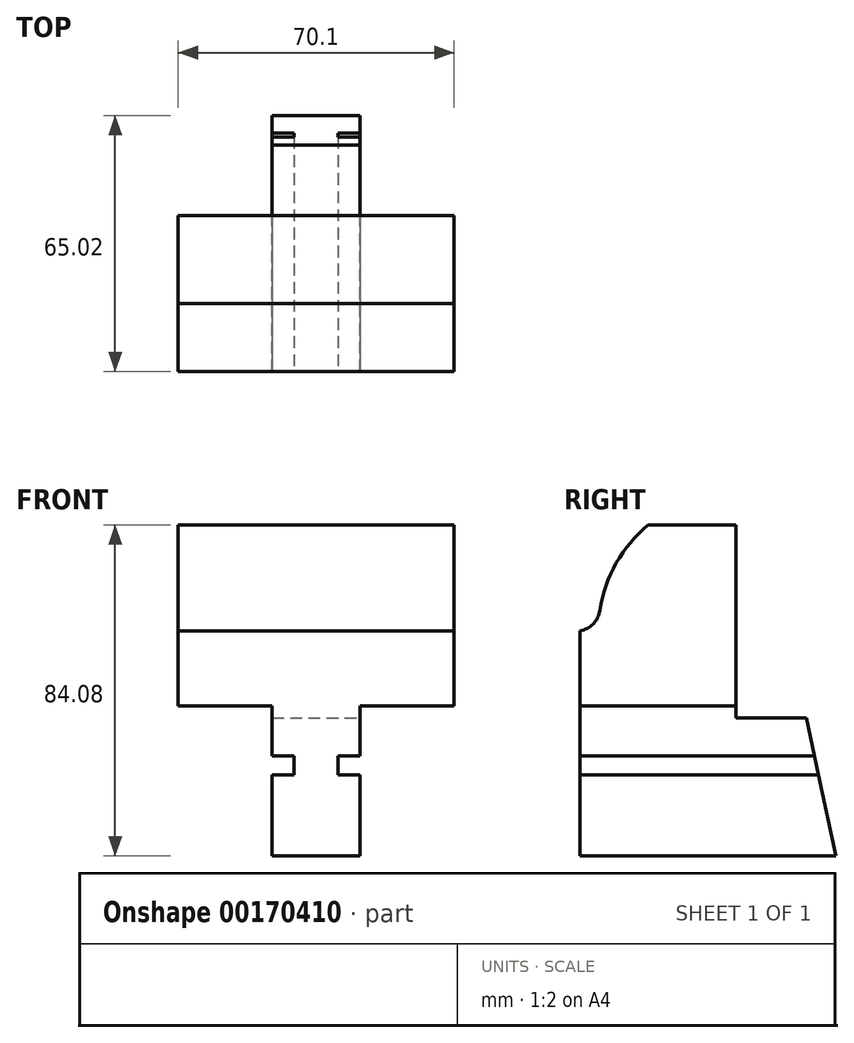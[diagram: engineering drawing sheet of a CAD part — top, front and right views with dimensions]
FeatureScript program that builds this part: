
annotation { "Feature Type Name" : "Feature", "Feature Type Description" : "" }
export const myFeature = defineFeature(function(context is Context, id is Id, definition is map)
    precondition{}
    {
        {
            var Q0;
            Q0=qCreatedBy(makeId("Right.planeOp"),FACE);
            var sketch = newSketch(context, id + "F0", { "sketchPlane" : qUnion([Q0])});
            skLineSegment(sketch, "E0.bottom", {"start": v(32.51, 42.04) * mm, "end": v(-32.51, 42.04) * mm});
            skLineSegment(sketch, "E0.top", {"start": v(32.51, -42.04) * mm, "end": v(-32.51, -42.04) * mm});
            skLineSegment(sketch, "E0.left", {"start": v(32.51, 42.04) * mm, "end": v(32.51, -42.04) * mm});
            skLineSegment(sketch, "E0.right", {"start": v(-32.51, 42.04) * mm, "end": v(-32.51, -42.04) * mm});
            skPoint(sketch, "E0.middle", {"position": v(0, 0) * mm});
            skSolve(sketch);
        }
        {
            var Q0;
            Q0=makeQuery(id+"F0.imprint","IMPRINT",FACE,{"disambiguationData":[TD([[makeQuery(id+"F0.imprint","IMPRINT",EDGE,{"derivedFrom":sQuery(id+"F0.wireOp",EDGE,"E0.bottom")}),1.0]])]});
            extrude(context, id + "F1", {"entities" : qUnion([Q0]), "depth" : 35.05 * mm, "hasSecondDirection" : true, "secondDirectionOppositeDirection" : true, "secondDirectionDepth" : 35.05 * mm});
        }
        {
            var Q0;
            Q0=qCreatedBy(makeId("Front.planeOp"),FACE);
            var sketch = newSketch(context, id + "F2", { "sketchPlane" : qUnion([Q0])});
            skLineSegment(sketch, "E1.bottom", {"start": v(-11.18, -3.94) * mm, "end": v(-78.23, -3.94) * mm});
            skLineSegment(sketch, "E1.top", {"start": v(-11.18, -87.81) * mm, "end": v(-78.23, -87.81) * mm});
            skLineSegment(sketch, "E1.left", {"start": v(-11.18, -3.94) * mm, "end": v(-11.18, -16.64) * mm});
            skLineSegment(sketch, "E1.right", {"start": v(-78.23, -3.94) * mm, "end": v(-78.23, -87.81) * mm});
            skLineSegment(sketch, "E2.bottom", {"start": v(11.18, -3.94) * mm, "end": v(75.68, -3.94) * mm});
            skLineSegment(sketch, "E2.top", {"start": v(11.18, -87.81) * mm, "end": v(75.68, -87.81) * mm});
            skLineSegment(sketch, "E2.left", {"start": v(11.18, -3.94) * mm, "end": v(11.18, -16.64) * mm});
            skLineSegment(sketch, "E2.right", {"start": v(75.68, -3.94) * mm, "end": v(75.68, -87.81) * mm});
            skLineSegment(sketch, "E3.bottom", {"start": v(-11.18, -16.64) * mm, "end": v(-5.59, -16.64) * mm});
            skLineSegment(sketch, "E3.top", {"start": v(-11.18, -21.46) * mm, "end": v(-5.59, -21.46) * mm});
            skLineSegment(sketch, "E3.right", {"start": v(-5.59, -16.64) * mm, "end": v(-5.59, -21.46) * mm});
            skLineSegment(sketch, "E4.trimOffspring", {"start": v(-11.18, -21.46) * mm, "end": v(-11.18, -87.81) * mm});
            skLineSegment(sketch, "E5.bottom", {"start": v(11.18, -16.64) * mm, "end": v(5.59, -16.64) * mm});
            skLineSegment(sketch, "E5.top", {"start": v(11.18, -21.46) * mm, "end": v(5.59, -21.46) * mm});
            skLineSegment(sketch, "E5.right", {"start": v(5.59, -16.64) * mm, "end": v(5.59, -21.46) * mm});
            skLineSegment(sketch, "E6.trimOffspring", {"start": v(11.18, -21.46) * mm, "end": v(11.18, -87.81) * mm});
            skSolve(sketch);
        }
        {
            var Q0;
            Q0 = qSketchRegion(id + "F2", true);
            extrude(context, id + "F3", {"entities" : qUnion([Q0]), "operationType" : NewBodyOperationType.REMOVE, "endBound" : BoundingType.SYMMETRIC, "oppositeDirection" : true, "depth" : 127 * mm});
        }
        {
            var Q0;
            Q0=qCreatedBy(makeId("Right.planeOp"),FACE);
            var sketch = newSketch(context, id + "F4", { "sketchPlane" : qUnion([Q0])});
            skLineSegment(sketch, "E7.bottom", {"start": v(7.11, -6.99) * mm, "end": v(84.5, -6.98) * mm});
            skLineSegment(sketch, "E7.top", {"start": v(7.11, 63.54) * mm, "end": v(84.5, 63.54) * mm});
            skLineSegment(sketch, "E7.left", {"start": v(7.11, -6.99) * mm, "end": v(7.11, 63.54) * mm});
            skLineSegment(sketch, "E7.right", {"start": v(84.5, -6.98) * mm, "end": v(84.5, 63.54) * mm});
            skSolve(sketch);
        }
        {
            var Q0;
            Q0 = qSketchRegion(id + "F4", true);
            extrude(context, id + "F5", {"entities" : qUnion([Q0]), "operationType" : NewBodyOperationType.REMOVE, "endBound" : BoundingType.SYMMETRIC, "oppositeDirection" : true, "depth" : 76.2 * mm});
        }
        {
            var Q0;
            Q0=makeQuery(id+"F3.boolean.opBoolean","COPY",FACE,{"derivedFrom":makeQuery(id+"F3.opExtrude","SWEPT_FACE",FACE,{"disambiguationData":[OSD([sQuery(id+"F2.wireOp",EDGE,"E6.trimOffspring")])]})});
            var sketch = newSketch(context, id + "F6", { "sketchPlane" : qUnion([Q0])});
            skLineSegment(sketch, "E8", {"start": v(32.51, -42.04) * mm, "end": v(22.86, 2.93) * mm});
            skLineSegment(sketch, "E9", {"start": v(22.86, 2.93) * mm, "end": v(55.12, 2.93) * mm});
            skLineSegment(sketch, "E10", {"start": v(55.12, 2.93) * mm, "end": v(58.15, -47.16) * mm});
            skLineSegment(sketch, "E11", {"start": v(58.15, -47.16) * mm, "end": v(32.51, -42.04) * mm});
            skSolve(sketch);
        }
        {
            var Q0;
            {var subQ0=sQuery(id+"F6.wireOp",EDGE,"E9");Q0=makeQuery(id+"F6.imprint","IMPRINT",FACE,{"disambiguationData":[TD([[makeQuery(id+"F6.imprint","IMPRINT",EDGE,{"derivedFrom":subQ0}),-1.0]])]});}
            var Q1;
            {var subQ1=sQuery(id+"F2.wireOp",EDGE,"E6.trimOffspring");var subQ2=makeQuery(id+"F3.opExtrude","SWEPT_FACE",FACE,{"disambiguationData":[OSD([subQ1])]});var subQ3=makeQuery(id+"F3.boolean.opBoolean","INTERSECT",EDGE,{"derivedFrom":[makeQuery(id+"F1.opExtrude","SWEPT_FACE",FACE,{"disambiguationData":[OSD([sQuery(id+"F0.wireOp",EDGE,"E0.left")])]}),subQ2]});Q1=makeQuery(id+"F6.imprint","IMPRINT",FACE,{"disambiguationData":[TD([[makeQuery(id+"F6.imprint","IMPRINT",EDGE,{"derivedFrom":subQ3}),1.0]])]});}
            extrude(context, id + "F7", {"entities" : qUnion([Q0, Q1]), "operationType" : NewBodyOperationType.REMOVE, "endBound" : BoundingType.SYMMETRIC, "depth" : 50.8 * mm});
        }
        {
            var Q0;
            Q0=qCreatedBy(makeId("Right.planeOp"),FACE);
            var sketch = newSketch(context, id + "F8", { "sketchPlane" : qUnion([Q0])});
            skArc(sketch, "E12", {"start": v(7.2, 50.16) * mm, "mid": v(-17.59, 39.9) * mm, "end": v(-27.85, 15.11) * mm});
            skLineSegment(sketch, "E13", {"start": v(7.2, 15.11) * mm, "end": v(-27.85, 15.11) * mm});
            skLineSegment(sketch, "E14", {"start": v(-27.85, 15.11) * mm, "end": v(-47.43, 15.11) * mm});
            skLineSegment(sketch, "E15", {"start": v(-47.43, 15.11) * mm, "end": v(-30.82, 66.05) * mm});
            skLineSegment(sketch, "E16", {"start": v(-30.82, 66.05) * mm, "end": v(7.2, 50.16) * mm});
            skLineSegment(sketch, "E17", {"start": v(7.2, 15.11) * mm, "end": v(7.2, 50.16) * mm});
            skSolve(sketch);
        }
        {
            var Q0;
            Q0=makeQuery(id+"F8.imprint","IMPRINT",FACE,{"disambiguationData":[TD([[makeQuery(id+"F8.imprint","IMPRINT",EDGE,{"derivedFrom":sQuery(id+"F8.wireOp",EDGE,"E12")}),-1.0]])]});
            extrude(context, id + "F9", {"entities" : qUnion([Q0]), "operationType" : NewBodyOperationType.REMOVE, "endBound" : BoundingType.SYMMETRIC, "oppositeDirection" : true, "depth" : 76.2 * mm});
        }
        {
            var Q0;
            Q0=makeQuery(id+"F9.boolean.opBoolean","COPY",EDGE,{"derivedFrom":makeQuery(id+"F9.opExtrude","SWEPT_EDGE",EDGE,{"disambiguationData":[OSD([sQuery(id+"F8.wireOp",EDGE,"E12"),sQuery(id+"F8.wireOp",EDGE,"E13"),sQuery(id+"F8.wireOp",EDGE,"E14")])]})});
            fillet(context, id + "F10", {"entities" : qUnion([Q0]), "radius" : 6.35 * mm, "tangentPropagation" : true, "allowEdgeOverflow" : false});
        }
    });
